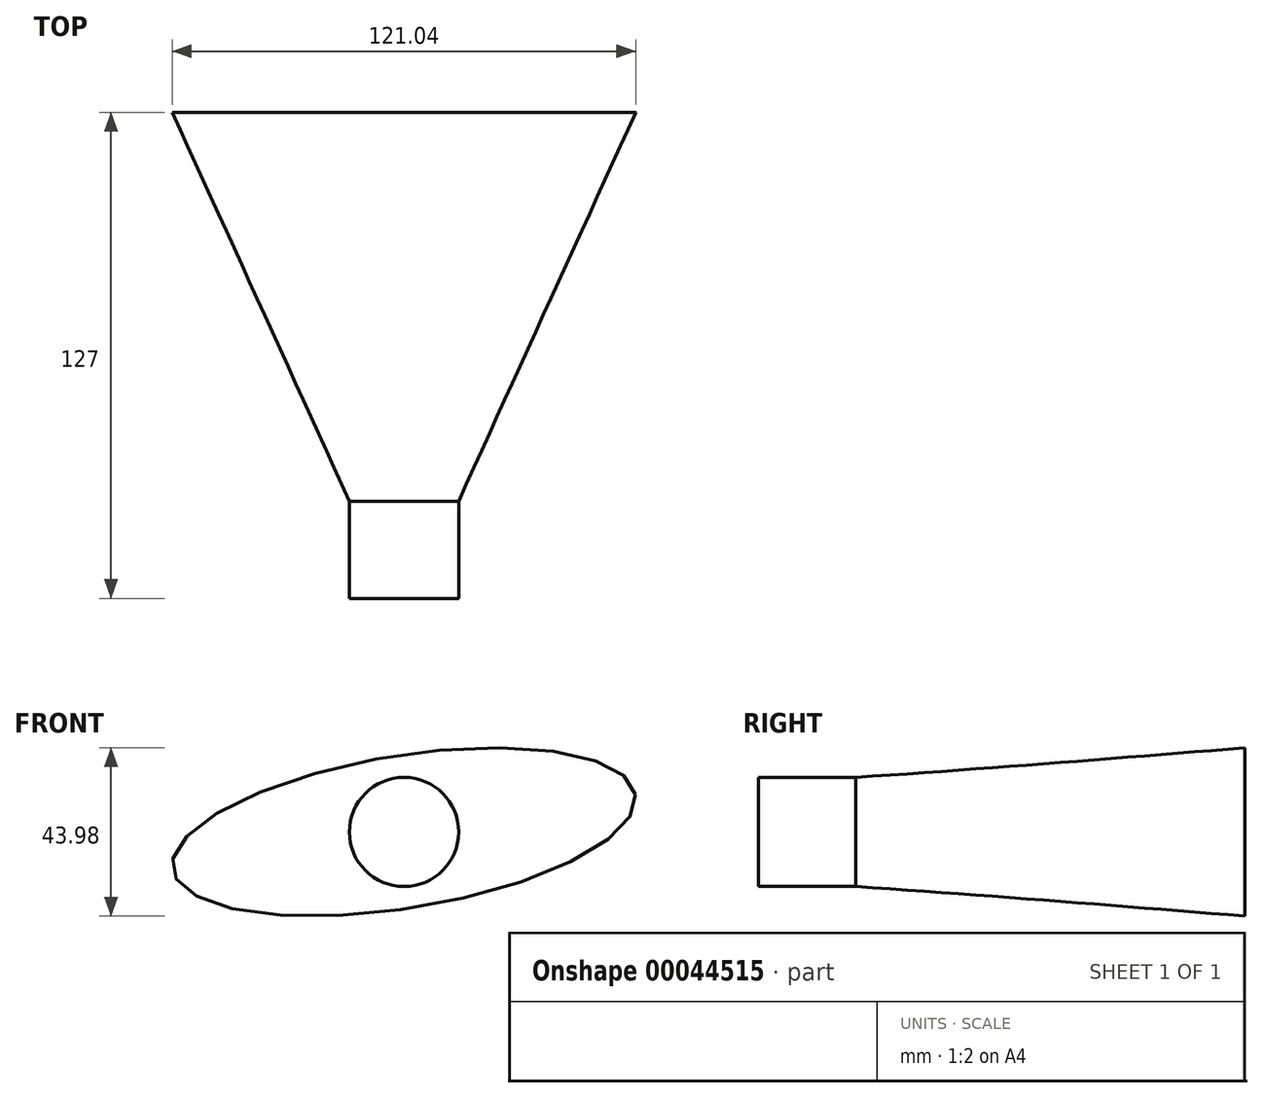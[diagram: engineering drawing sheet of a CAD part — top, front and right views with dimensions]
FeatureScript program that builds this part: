
annotation { "Feature Type Name" : "Feature", "Feature Type Description" : "" }
export const myFeature = defineFeature(function(context is Context, id is Id, definition is map)
    precondition{}
    {
        {
            var Q0;
            Q0=qCreatedBy(makeId("Front.planeOp"),FACE);
            var sketch = newSketch(context, id + "F0", { "sketchPlane" : qUnion([Q0])});
            skEllipse(sketch, "E0", {"center": v(0, 0) * mm, "majorRadius": 61.22 * mm, "minorRadius": 19.97 * mm, "majorAxis": v(0.99, 0.16)});
            skCircle(sketch, "E1", {"center": v(0, 0) * mm, "radius": 14.26 * mm});
            skSolve(sketch);
        }
        {
            var Q0;
            Q0=makeQuery(id+"F0.imprint","IMPRINT",FACE,{"disambiguationData":[TD([[makeQuery(id+"F0.imprint","IMPRINT",EDGE,{"derivedFrom":sQuery(id+"F0.wireOp",EDGE,"E1")}),1.0]])]});
            extrude(context, id + "F1", {"entities" : qUnion([Q0]), "depth" : 101.6 * mm});
        }
        {
            var Q0;
            Q0=qCreatedBy(makeId("Front.planeOp"),FACE);
            var sketch = newSketch(context, id + "F2", { "sketchPlane" : qUnion([Q0])});
            skEllipse(sketch, "E2.0", {"center": v(0, 0) * mm, "majorRadius": 61.22 * mm, "minorRadius": 19.97 * mm, "majorAxis": v(0.99, 0.16)});
            skSolve(sketch);
        }
        {
            var Q1;
            Q1=makeQuery(id+"F2.imprint","IMPRINT",FACE,{"disambiguationData":[TD([[makeQuery(id+"F2.imprint","IMPRINT",EDGE,{"derivedFrom":sQuery(id+"F2.wireOp",EDGE,"E2.0")}),1.0]])]});
            var Q2;
            Q2=makeQuery(id+"F1.opExtrude","CAP_FACE",FACE,{"disambiguationData":[OSD([sQuery(id+"F0.wireOp",EDGE,"E1")])],"isStart":false});
            loft(context, id + "F3", {"operationType" : NewBodyOperationType.ADD, "sheetProfilesArray" : [{ "sheetProfileEntities" : qUnion([Q1]) }, { "sheetProfileEntities" : qUnion([Q2]) }]});
        }
        {
            var Q0;
            Q0=makeQuery(id+"F1.opExtrude","CAP_FACE",FACE,{"disambiguationData":[OSD([sQuery(id+"F0.wireOp",EDGE,"E1")])],"isStart":false});
            extrude(context, id + "F4", {"entities" : qUnion([Q0]), "operationType" : NewBodyOperationType.ADD, "depth" : 25.4 * mm});
        }
    });
